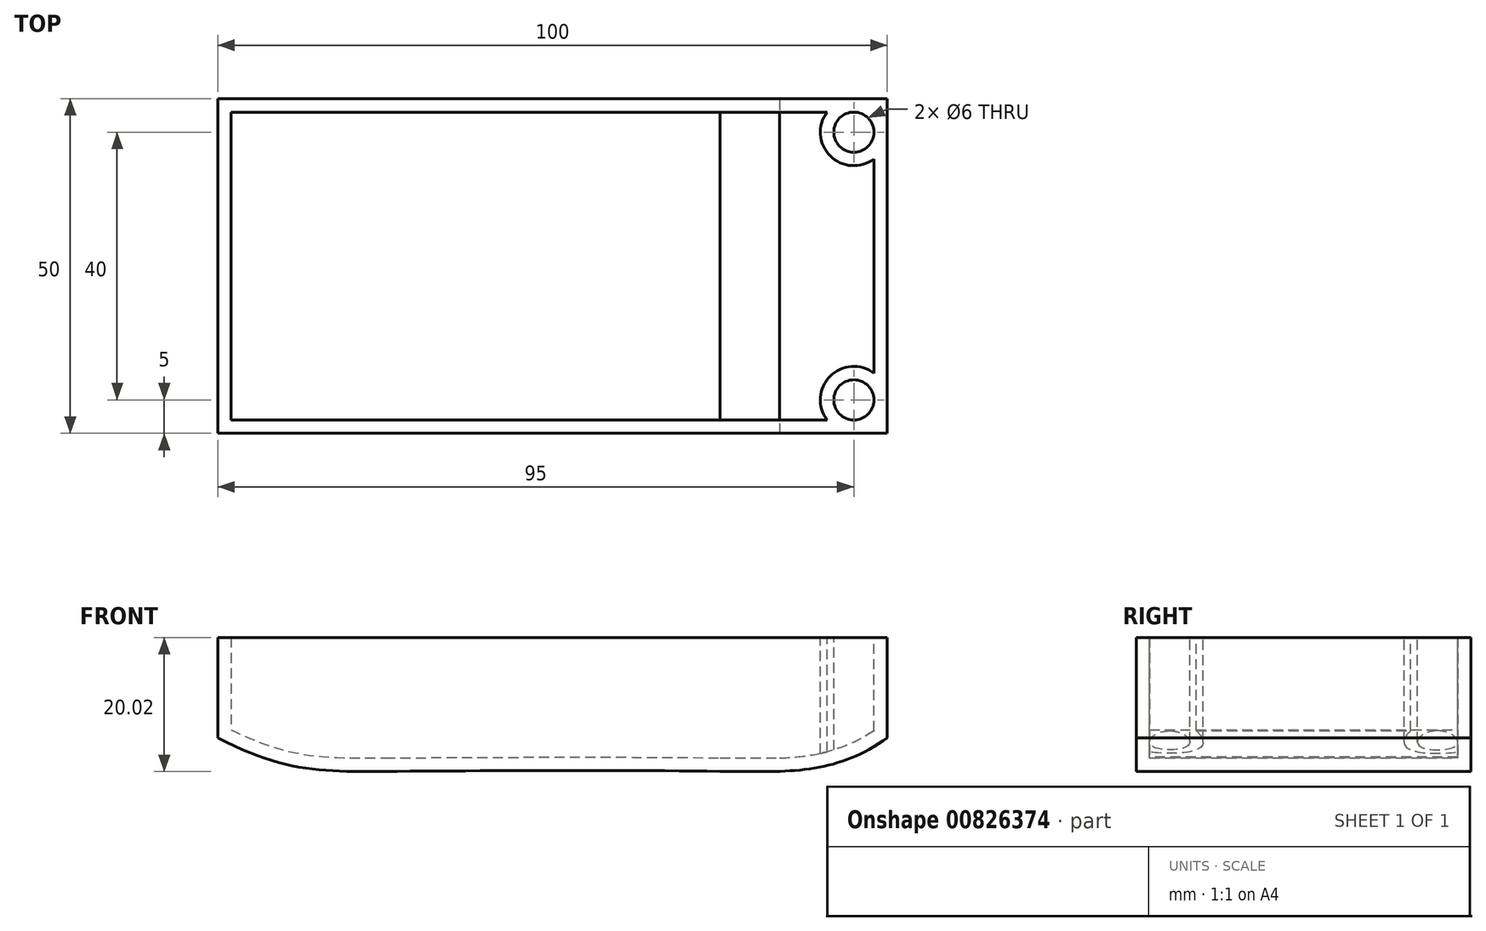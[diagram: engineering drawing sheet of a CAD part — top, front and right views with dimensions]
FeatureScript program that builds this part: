
annotation { "Feature Type Name" : "Feature", "Feature Type Description" : "" }
export const myFeature = defineFeature(function(context is Context, id is Id, definition is map)
    precondition{}
    {
        {
            var Q0;
            Q0=qCreatedBy(makeId("Front.planeOp"),FACE);
            var sketch = newSketch(context, id + "F0", { "sketchPlane" : qUnion([Q0])});
            skFitSpline(sketch, "E0", {"points": [v(-50, -5) * mm, v(-25, -10) * mm, v(25, -10) * mm, v(50, -5) * mm], "startDerivative": vector(102.02, -52.54) * mm, "endDerivative": vector(78.25, 55.56) * mm});
            skLineSegment(sketch, "E1.bottom", {"start": v(-50, 10) * mm, "end": v(50, 10) * mm});
            skLineSegment(sketch, "E1.top", {"start": v(-25, -10) * mm, "end": v(33.95, -10) * mm});
            skLineSegment(sketch, "E1.left", {"start": v(-50, 10) * mm, "end": v(-50, -5) * mm});
            skLineSegment(sketch, "E1.right", {"start": v(50, 10) * mm, "end": v(50, -5) * mm});
            skPoint(sketch, "E2.orphan", {"position": v(-50, -10) * mm});
            skPoint(sketch, "E3.orphan", {"position": v(50, -10) * mm});
            skSolve(sketch);
        }
        {
            var Q0;
            Q0=makeQuery(id+"F0.imprint","IMPRINT",FACE,{"disambiguationData":[TD([[makeQuery(id+"F0.imprint","IMPRINT",EDGE,{"derivedFrom":sQuery(id+"F0.wireOp",EDGE,"E1.bottom")}),-1.0]])]});
            extrude(context, id + "F1", {"entities" : qUnion([Q0]), "endBound" : BoundingType.SYMMETRIC, "depth" : 50 * mm, "offsetDistance" : 25 * mm});
        }
        {
            var Q0;
            Q0=makeQuery(id+"F1.opExtrude","SWEPT_FACE",FACE,{"disambiguationData":[OSD([sQuery(id+"F0.wireOp",EDGE,"E1.bottom")])]});
            shell(context, id + "F2", {"entities" : qUnion([Q0]), "thickness" : 2 * mm});
        }
        {
            var Q0;
            Q0=makeQuery(id+"F1.opExtrude","SWEPT_FACE",FACE,{"disambiguationData":[OSD([sQuery(id+"F0.wireOp",EDGE,"E1.bottom")])]});
            var sketch = newSketch(context, id + "F3", { "sketchPlane" : qUnion([Q0])});
            skCircle(sketch, "E4", {"center": v(45, 20) * mm, "radius": 5 * mm});
            skCircle(sketch, "E5", {"center": v(45, 20) * mm, "radius": 3 * mm});
            skSolve(sketch);
        }
        {
            var Q0;
            {var subQ0=sQuery(id+"F3.wireOp",EDGE,"E5");var subQ1=sQuery(id+"F0.wireOp",EDGE,"E1.bottom");var subQ4=makeQuery(id+"F2.opShell","OFFSET_EDGE",EDGE,{"disambiguationData":[OSD([subQ1]),TDD([makeQuery(id+"F1.opExtrude","CAP_EDGE",EDGE,{"disambiguationData":[OSD([subQ1])],"isStart":true})])]});var subQ5=makeQuery(id+"F3.imprint","INTERSECT",VERTEX,{"derivedFrom":[subQ4,subQ0]});Q0=makeQuery(id+"F3.imprint","IMPRINT",FACE,{"disambiguationData":[TD([[makeQuery(id+"F3.imprint","IMPRINT",EDGE,{"disambiguationData":[TD([[subQ5,1.0]])],"derivedFrom":subQ0}),-1.0]])]});}
            var Q1;
            {var subQ0=sQuery(id+"F3.wireOp",EDGE,"E4");var subQ1=sQuery(id+"F0.wireOp",EDGE,"E1.bottom");var subQ2=makeQuery(id+"F2.opShell","OFFSET_EDGE",EDGE,{"disambiguationData":[OSD([subQ1]),TDD([makeQuery(id+"F1.opExtrude","CAP_EDGE",EDGE,{"disambiguationData":[OSD([subQ1])],"isStart":true})])]});var subQ3=makeQuery(id+"F3.imprint","INTERSECT",VERTEX,{"derivedFrom":[subQ2,subQ0]});Q1=makeQuery(id+"F3.imprint","IMPRINT",FACE,{"disambiguationData":[TD([[makeQuery(id+"F3.imprint","IMPRINT",EDGE,{"disambiguationData":[TD([[subQ3,-1.0]])],"derivedFrom":subQ2}),-1.0]])]});}
            extrude(context, id + "F4", {"entities" : qUnion([Q0, Q1]), "endBound" : BoundingType.UP_TO_NEXT, "oppositeDirection" : true, "depth" : 25 * mm, "offsetDistance" : 25 * mm});
        }
        {
            var Q0;
            Q0=makeQuery(id+"F4.opExtrude","SWEPT_BODY",BODY,{"disambiguationData":[OSD([sQuery(id+"F0.wireOp",EDGE,"E1.bottom"),sQuery(id+"F0.wireOp",EDGE,"E1.right"),sQuery(id+"F3.wireOp",EDGE,"E5")])]});
            var Q1;
            Q1=makeQuery(id+"F4.opExtrude","SWEPT_BODY",BODY,{"disambiguationData":[OSD([sQuery(id+"F0.wireOp",EDGE,"E1.bottom"),sQuery(id+"F0.wireOp",EDGE,"E1.right"),sQuery(id+"F3.wireOp",EDGE,"E4"),sQuery(id+"F3.wireOp",EDGE,"E5")])]});
            var Q2;
            Q2=qCreatedBy(makeId("Front.planeOp"),FACE);
            mirror(context, id + "F5", {"operationType" : NewBodyOperationType.ADD, "entities" : qUnion([Q0, Q1]), "mirrorPlane" : qUnion([Q2])});
        }
    });
